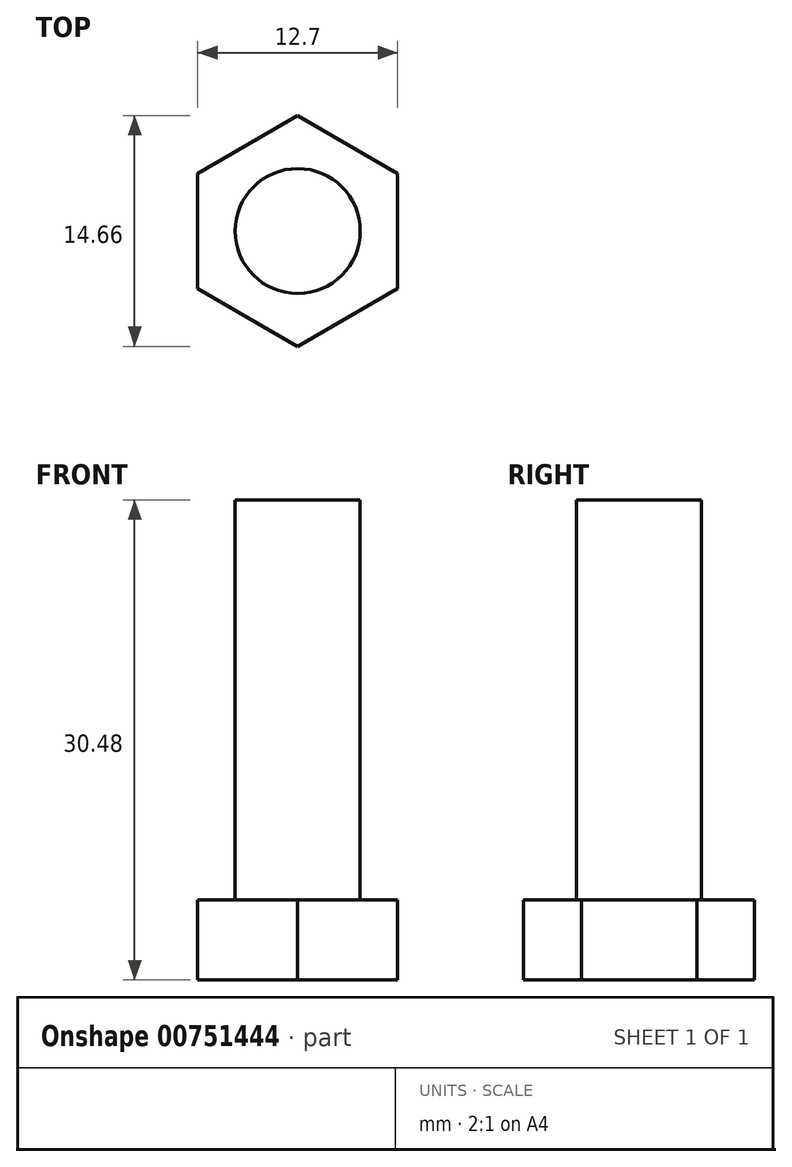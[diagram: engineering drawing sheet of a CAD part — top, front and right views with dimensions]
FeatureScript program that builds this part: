
annotation { "Feature Type Name" : "Feature", "Feature Type Description" : "" }
export const myFeature = defineFeature(function(context is Context, id is Id, definition is map)
    precondition{}
    {
        {
            var Q0;
            Q0=qCreatedBy(makeId("Top.planeOp"),FACE);
            var sketch = newSketch(context, id + "F0", { "sketchPlane" : qUnion([Q0])});
            skCircle(sketch, "E0.cCircle", {"center": v(0, 0) * mm, "radius": 6.35 * mm, "construction": true});
            skLineSegment(sketch, "E0.0", {"start": v(6.35, 3.67) * mm, "end": v(6.35, -3.67) * mm});
            skLineSegment(sketch, "E0.1", {"start": v(6.35, -3.67) * mm, "end": v(0, -7.33) * mm});
            skLineSegment(sketch, "E0.2", {"start": v(0, -7.33) * mm, "end": v(-6.35, -3.67) * mm});
            skLineSegment(sketch, "E0.3", {"start": v(-6.35, -3.67) * mm, "end": v(-6.35, 3.67) * mm});
            skLineSegment(sketch, "E0.4", {"start": v(-6.35, 3.67) * mm, "end": v(0, 7.33) * mm});
            skLineSegment(sketch, "E0.5", {"start": v(0, 7.33) * mm, "end": v(6.35, 3.67) * mm});
            skPoint(sketch, "E0.0.midPoint", {"position": v(6.35, 0) * mm});
            skCircle(sketch, "E1", {"center": v(0, 0) * mm, "radius": 3.97 * mm});
            skSolve(sketch);
        }
        {
            var Q0;
            Q0=makeQuery(id+"F0.imprint","IMPRINT",FACE,{"disambiguationData":[TD([[makeQuery(id+"F0.imprint","IMPRINT",EDGE,{"derivedFrom":sQuery(id+"F0.wireOp",EDGE,"E0.0")}),-1.0]])]});
            extrude(context, id + "F1", {"entities" : qUnion([Q0]), "depth" : 5.08 * mm, "offsetDistance" : 25.4 * mm});
        }
        {
            var Q0;
            Q0=makeQuery(id+"F0.imprint","IMPRINT",FACE,{"disambiguationData":[TD([[makeQuery(id+"F0.imprint","IMPRINT",EDGE,{"derivedFrom":sQuery(id+"F0.wireOp",EDGE,"E1")}),1.0]])]});
            extrude(context, id + "F2", {"entities" : qUnion([Q0]), "operationType" : NewBodyOperationType.ADD, "depth" : 30.48 * mm, "offsetDistance" : 25.4 * mm});
        }
    });
